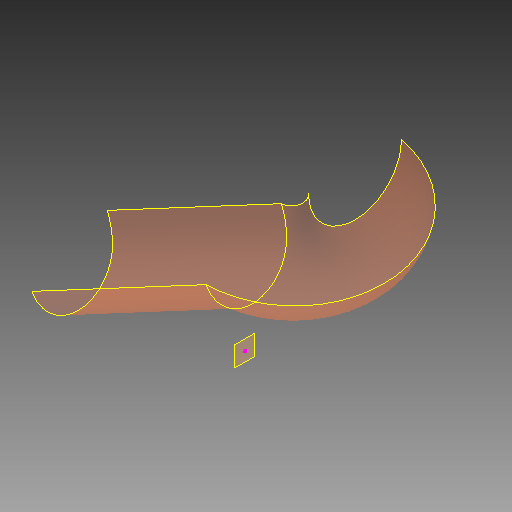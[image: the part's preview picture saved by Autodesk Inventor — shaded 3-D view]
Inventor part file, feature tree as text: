
AUTODESK INVENTOR PART (.ipt)
format: ipt  version: 2017 (Build 210142000, 142)  size: 143,360 bytes
history: native  units: in
note: dims shown in document units (in); Inventor stores cm internally (conversion verified against a paired STEP export)
features: plane x2, sketch x2, other x1, sweep x1
ambient origin geometry x8: Origin, YZ Plane, XZ Plane, XY Plane, X Axis, Y Axis, Z Axis, Center Point
bodies: Body1 (feature_tree)
feature tree (6):
  plane  "Work Plane8"
  plane  "Work Plane13"
  sketch  "Sketch9"  dims[d18=4.0in d19=4.0in d26=2.75in d33=0.0in d34=0.0in]
  sketch  "3D Sketch1"
  other  "Srf1"
  sweep  "SweepSrf1"
